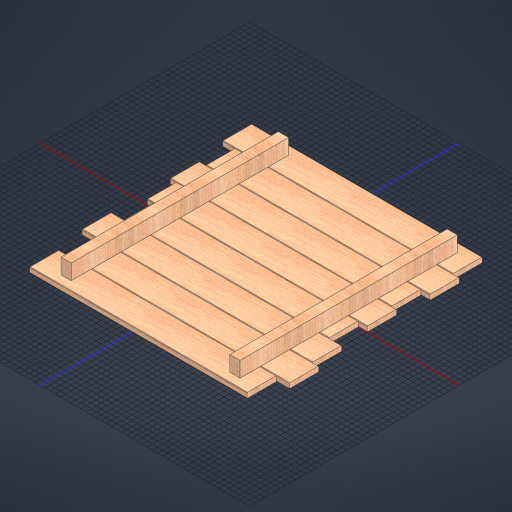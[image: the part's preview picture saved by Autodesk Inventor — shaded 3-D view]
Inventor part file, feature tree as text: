
AUTODESK INVENTOR PART (.ipt)
format: ipt  version: 2023.2 (Build 272271030, 271C)  size: 613,888 bytes
history: native  units: mm
features: extrude x9, sketch x2
ambient origin geometry x8: Origin, YZ Plane, XZ Plane, XY Plane, X Axis, Y Axis, Z Axis, Center Point
bodies: Volumenkörper1 (feature_tree)
feature tree (11):
  sketch  "Skizze1"  dims[d0=20.0mm d1=115.0mm]
  extrude  "Extrusion1"  Depth=115.0mm
  extrude  "Extrusion3"  Depth=60.0mm TaperAngle=0.0deg
  extrude  "Extrusion2"  Depth=425.0mm TaperAngle=0.0deg
  extrude  "Extrusion4"  Depth=425.0mm TaperAngle=0.0deg
  extrude  "Extrusion5"  Depth=460.0mm TaperAngle=0.0deg
  extrude  "Extrusion6"  Depth=425.0mm TaperAngle=0.0deg
  extrude  "Extrusion7"  Depth=60.0mm TaperAngle=0.0deg
  extrude  "Extrusion9"  Depth=60.0mm
  extrude  "Extrusion8"  Depth=60.0mm
  sketch  "Skizze2"  dims[d2=450.0mm d3=400.0mm d4=0.0mm d5=0.0mm d6=500.0mm d7=350.0mm d8=0.0mm d9=0.0mm d10=475.0mm d11=425.0mm d12=0.0mm d13=0.0mm d14=425.0mm d15=375.0mm d16=0.0mm d17=0.0mm d18=460.0mm d19=400.0mm d20=0.0mm d21=0.0mm d22=440.0mm d23=425.0mm d24=0.0mm d25=0.0mm d26=475.0mm d27=400.0mm d28=0.0mm d29=0.0mm d30=2.0mm d31=2.0mm d32=2.0mm d33=2.0mm d34=2.0mm d35=2.0mm d36=2.0mm d37=2.0mm d38=2.0mm d39=2.0mm d40=2.0mm d41=2.0mm d42=2.0mm d43=2.0mm d44=2.0mm d45=2.0mm d46=2.0mm d47=2.0mm d48=2.0mm d49=2.0mm d50=2.0mm d51=2.0mm d52=2.0mm d53=2.0mm d54=2.0mm d55=2.0mm d56=2.0mm d57=2.0mm d58=2.0mm d59=2.0mm d60=2.0mm d61=2.0mm d62=2.0mm d63=2.0mm d64=2.0mm d65=2.0mm d66=2.0mm d67=2.0mm d68=2.0mm d69=2.0mm d70=2.0mm d71=2.0mm d72=2.0mm d73=2.0mm d74=2.0mm d75=2.0mm d76=2.0mm d77=2.0mm d78=2.0mm d79=2.0mm d80=2.0mm d81=2.0mm d82=40.0mm d83=40.0mm d84=850.0mm d85=700.0mm d88=60.0mm d89=0.0mm d90=2.0mm d91=2.0mm d92=2.0mm d93=2.0mm d94=2.0mm d95=2.0mm d96=2.0mm d97=2.0mm d98=450.0mm d99=450.0mm d100=0.0mm d101=0.0mm d102=2.0mm d103=2.0mm d104=2.0mm d105=2.0mm]
